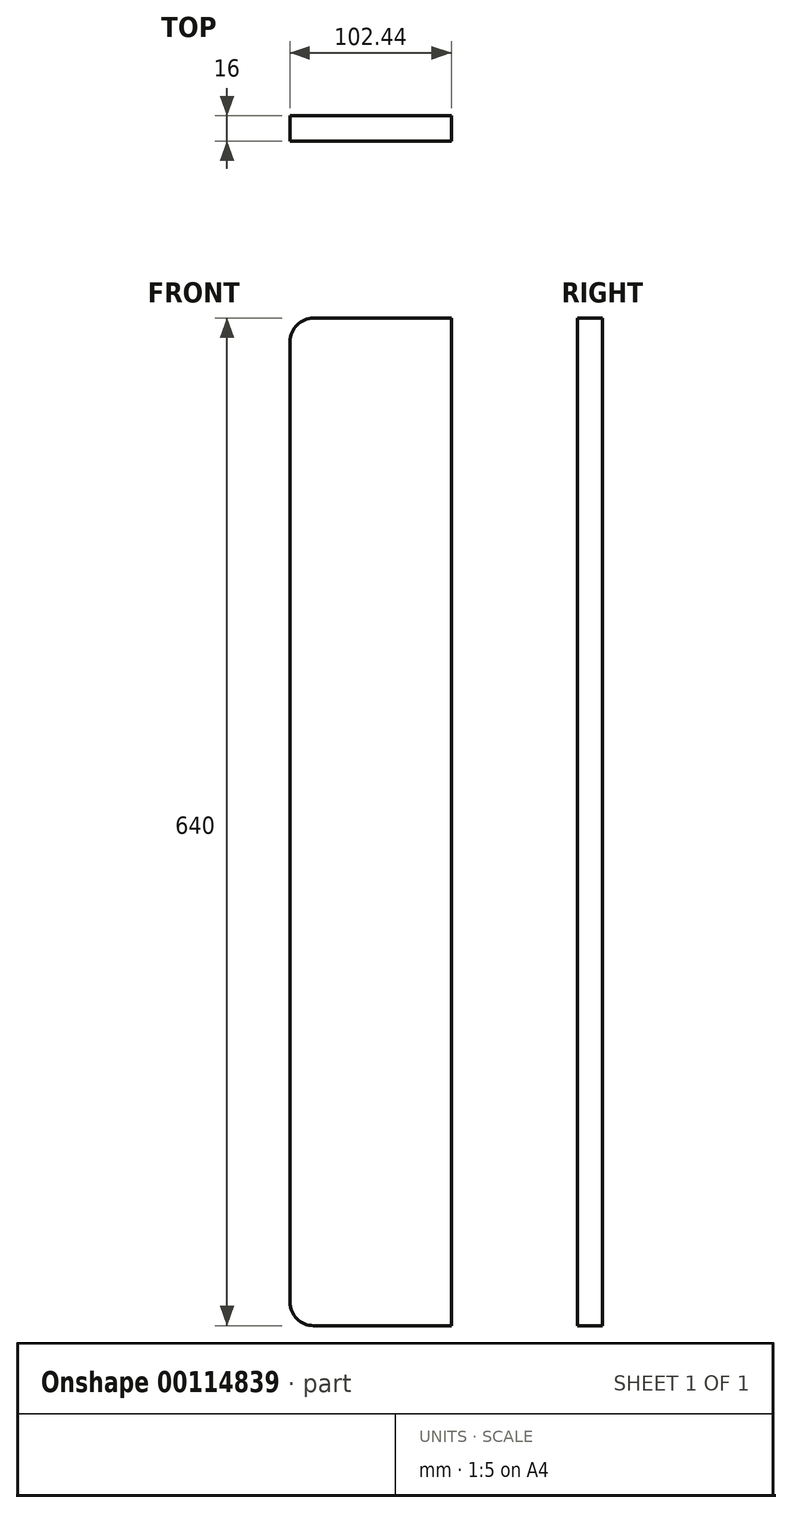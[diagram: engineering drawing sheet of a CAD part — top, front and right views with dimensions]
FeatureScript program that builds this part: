
annotation { "Feature Type Name" : "Feature", "Feature Type Description" : "" }
export const myFeature = defineFeature(function(context is Context, id is Id, definition is map)
    precondition{}
    {
        {
            var Q0;
            Q0=qCreatedBy(makeId("Front.planeOp"),FACE);
            var sketch = newSketch(context, id + "F0", { "sketchPlane" : qUnion([Q0])});
            skLineSegment(sketch, "E0.bottom", {"start": v(15, 640) * mm, "end": v(102.44, 640) * mm});
            skLineSegment(sketch, "E0.top", {"start": v(15, 0) * mm, "end": v(102.44, 0) * mm});
            skLineSegment(sketch, "E0.left", {"start": v(0, 625) * mm, "end": v(0, 15) * mm});
            skPoint(sketch, "E1.visualSharp", {"position": v(0, 640) * mm});
            skArc(sketch, "E1.filletArc", {"start": v(15, 640) * mm, "mid": v(4.4, 635.6) * mm, "end": v(0, 625) * mm});
            skPoint(sketch, "E2.visualSharp", {"position": v(0, 0) * mm});
            skArc(sketch, "E2.filletArc", {"start": v(0, 15) * mm, "mid": v(4.4, 4.4) * mm, "end": v(15, 0) * mm});
            skLineSegment(sketch, "E3", {"start": v(102.44, 640) * mm, "end": v(102.44, 0) * mm});
            skLineSegment(sketch, "E4", {"start": v(0, 285.28) * mm, "end": v(102.44, 285.28) * mm, "construction": true});
            skSolve(sketch);
        }
        {
            var Q0;
            Q0=makeQuery(id+"F0.imprint","IMPRINT",FACE,{"disambiguationData":[TD([[makeQuery(id+"F0.imprint","IMPRINT",EDGE,{"derivedFrom":sQuery(id+"F0.wireOp",EDGE,"E0.bottom")}),-1.0]])]});
            extrude(context, id + "F1", {"entities" : qUnion([Q0]), "depth" : 16 * mm});
        }
    });
